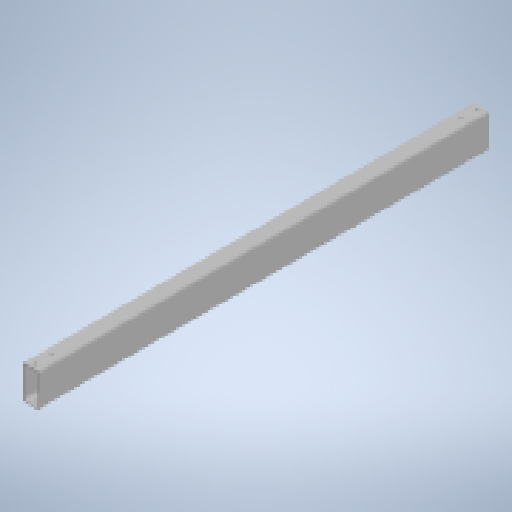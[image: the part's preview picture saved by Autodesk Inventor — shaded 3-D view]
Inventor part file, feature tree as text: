
AUTODESK INVENTOR PART (.ipt)
format: ipt  version: 2023 (Build 270158000, 158)  size: 205,312 bytes
history: native  units: in
note: dims shown in document units (in); Inventor stores cm internally (conversion verified against a paired STEP export)
features: extrude x2, sketch x2, shell x1, fillet x1
ambient origin geometry x8: Origin, YZ Plane, XZ Plane, XY Plane, X Axis, Y Axis, Z Axis, Center Point
bodies: Solid1 (feature_tree)
feature tree (6):
  extrude  "Extrusion1"  Depth=2.0in
  shell  "Shell1"  Thickness=54.0in
  fillet  "Fillet1"  Radius=0.125in
  extrude  "Extrusion2"  Depth=0.25in
  sketch  "Sketch1"  dims[d0=4.0in d1=2.0in d2=54.0in d3=0.0in d4=0.125in]
  sketch  "Sketch2"  dims[d5=0.25in d6=0.315in d7=1.5in d8=1.9685in d9=49.0in d10=0.0in]
